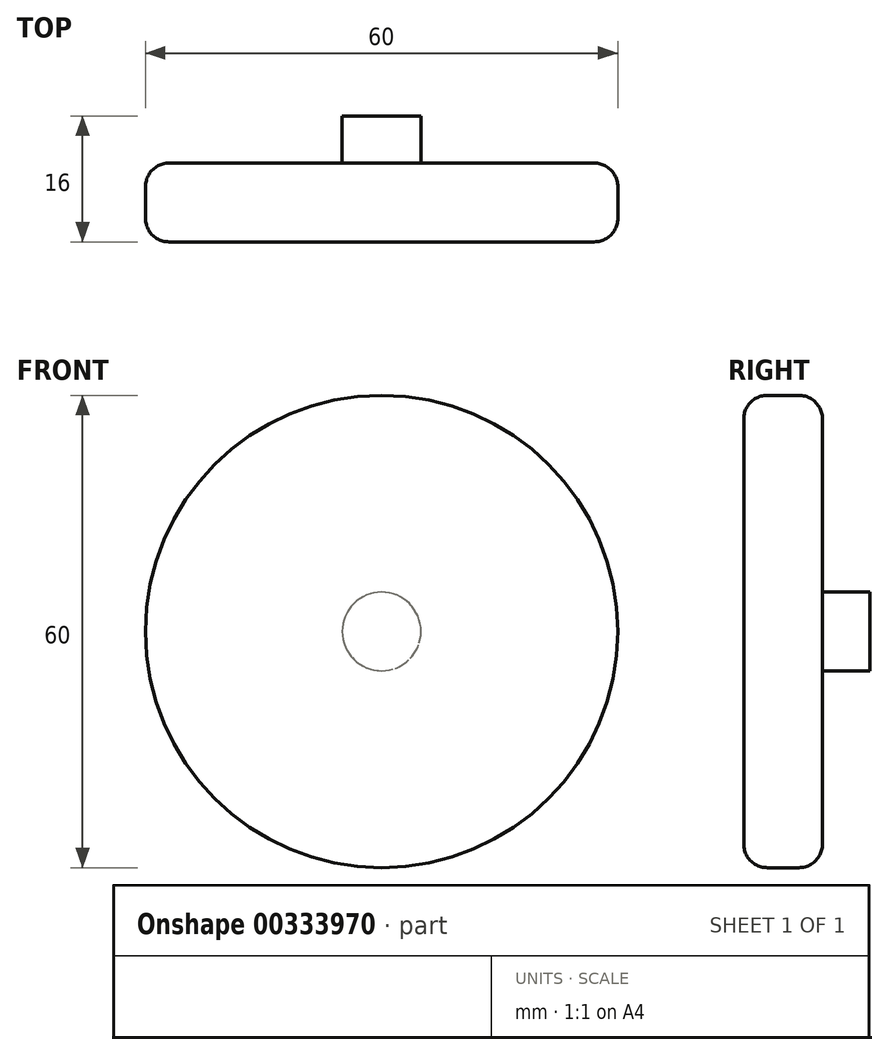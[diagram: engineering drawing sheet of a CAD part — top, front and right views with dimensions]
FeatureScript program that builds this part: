
annotation { "Feature Type Name" : "Feature", "Feature Type Description" : "" }
export const myFeature = defineFeature(function(context is Context, id is Id, definition is map)
    precondition{}
    {
        {
            var Q0;
            Q0=qCreatedBy(makeId("Front.planeOp"),FACE);
            var sketch = newSketch(context, id + "F0", { "sketchPlane" : qUnion([Q0])});
            skCircle(sketch, "E0", {"center": v(0, 0) * mm, "radius": 30 * mm});
            skSolve(sketch);
        }
        {
            var Q0;
            Q0=makeQuery(id+"F0.imprint","IMPRINT",FACE,{"disambiguationData":[TD([[makeQuery(id+"F0.imprint","IMPRINT",EDGE,{"derivedFrom":sQuery(id+"F0.wireOp",EDGE,"E0")}),1.0]])]});
            extrude(context, id + "F1", {"entities" : qUnion([Q0]), "depth" : 10 * mm});
        }
        {
            var Q0;
            Q0=makeQuery(id+"F1.opExtrude","CAP_EDGE",EDGE,{"disambiguationData":[OSD([sQuery(id+"F0.wireOp",EDGE,"E0")])],"isStart":false});
            var Q1;
            Q1=makeQuery(id+"F1.opExtrude","CAP_EDGE",EDGE,{"disambiguationData":[OSD([sQuery(id+"F0.wireOp",EDGE,"E0")])],"isStart":true});
            fillet(context, id + "F2", {"entities" : qUnion([Q0, Q1]), "radius" : 3 * mm, "tangentPropagation" : true, "allowEdgeOverflow" : false});
        }
        {
            var Q0;
            Q0=makeQuery(id+"F1.opExtrude","CAP_FACE",FACE,{"disambiguationData":[OSD([sQuery(id+"F0.wireOp",EDGE,"E0")])],"isStart":true});
            var sketch = newSketch(context, id + "F3", { "sketchPlane" : qUnion([Q0])});
            skCircle(sketch, "E1", {"center": v(0, 0) * mm, "radius": 5 * mm});
            skSolve(sketch);
        }
        {
            var Q0;
            Q0 = qSketchRegion(id + "F3", true);
            extrude(context, id + "F4", {"entities" : qUnion([Q0]), "operationType" : NewBodyOperationType.ADD, "depth" : 6 * mm});
        }
    });
